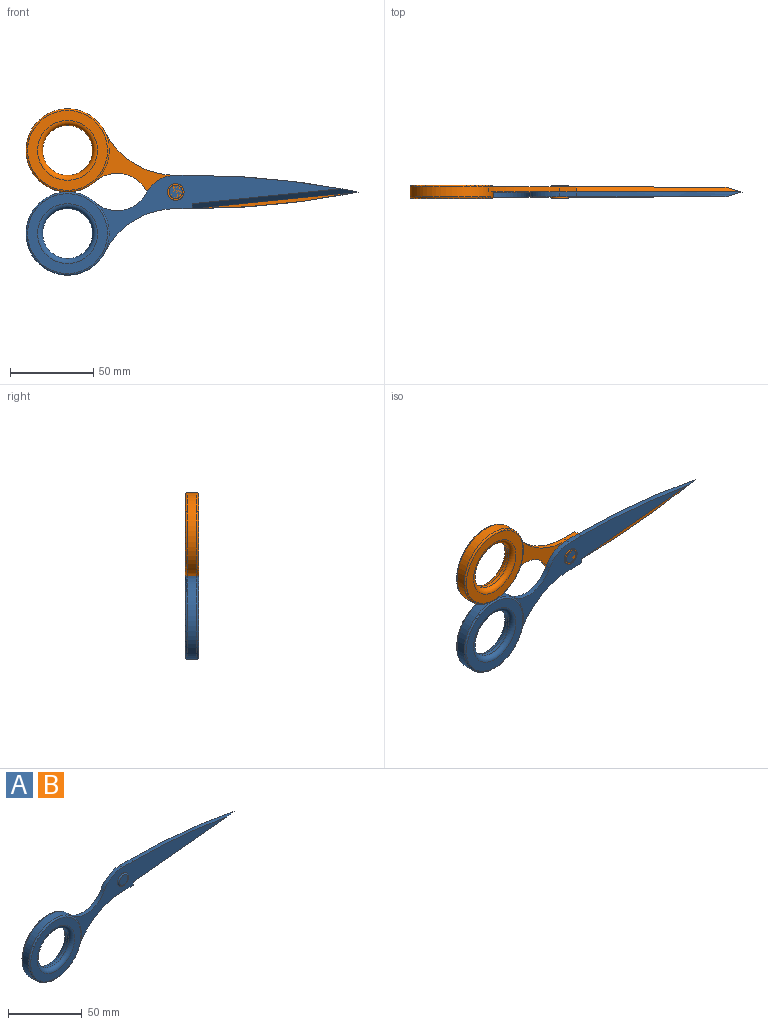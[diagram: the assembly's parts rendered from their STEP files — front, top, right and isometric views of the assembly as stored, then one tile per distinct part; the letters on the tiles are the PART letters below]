
ASSEMBLY  parts=2 mates=1
PART A: 22 faces, bbox 201.6x8x62.1 mm
  f0: plane 147.74x46.27mm, normal (0,-1,0), area 1612.7mm2, adj f2,f3,f4,f6,f7,f8,f15,f16
  f1: plane 157.99x46.27mm, normal (0,1,0), area 1896mm2, adj f2,f3,f4,f5,f6,f7,f8,f13
  f2: plane 10x3mm, normal (0,0,1), area 30mm2, adj f0,f1,f3,f8
  f3: cylinder r=20mm len=17.32mm, axis (0,1,0), area 62.8mm2, adj f0,f1,f2,f4
  f4: cylinder r=20mm len=31.17mm, axis (0,1,0), area 110.2mm2, adj f0,f1,f3,f5
  f5: cylinder r=25mm len=50mm, axis (0,1,0), area 843.7mm2, adj f1,f4,f6,f19,f20
  f6: cylinder r=47.81mm len=42.68mm, axis (0,1,0), area 158.3mm2, adj f0,f1,f5,f7
  f7: plane 10x3mm, normal (0,0,-1), area 30mm2, adj f0,f1,f6,f16
  f8: cylinder r=500mm len=99.5mm, axis (0,1,0), area 285mm2, adj f0,f1,f2,f15
  f9: plane 48x48mm, normal (0,1,0), area 791.7mm2, adj f18,f19
  f10: cylinder r=15mm len=30mm, axis (0,1,0), area 188.5mm2, adj f17,f18
  f11: plane 48x48mm, normal (0,-1,0), area 791.7mm2, adj f17,f20
  f12: plane 10x10mm, normal (0,1,0), area 78.5mm2, adj f13
  f13: cylinder r=5mm len=10mm, axis (0,1,0), area 125.7mm2, adj f1,f12
  f14: plane 8x8mm, normal (0,-1,0), area 50.3mm2, adj f21
  f15: plane 99.5x11.97mm, normal (0.07,-0.71,-0.71), area 401.7mm2, adj f0,f1,f8,f16
  f16: plane 3x3mm, normal (1,0,0), area 4.5mm2, adj f0,f7,f15
  f17: torus R=18mm, axis (0,-1,0), area 476.4mm2, adj f10,f11
  f18: torus R=18mm, axis (0,-1,0), area 476.4mm2, adj f9,f10
  f19: torus R=24mm, axis (0,-1,0), area 243.2mm2, adj f5,f9
  f20: torus R=24mm, axis (0,-1,0), area 243.2mm2, adj f0,f5,f11
  f21: torus R=4mm, axis (0,-1,0), area 45.8mm2, adj f0,f14
PART B: same geometry as A
PLACE A at identity fixed
PLACE B rot(axis=(1,0,0),180deg) t=(0,0,0)mm
MATE revolute A.f13 <-> B.f13  axis (0,-1,0) through (0,0,0)mm
